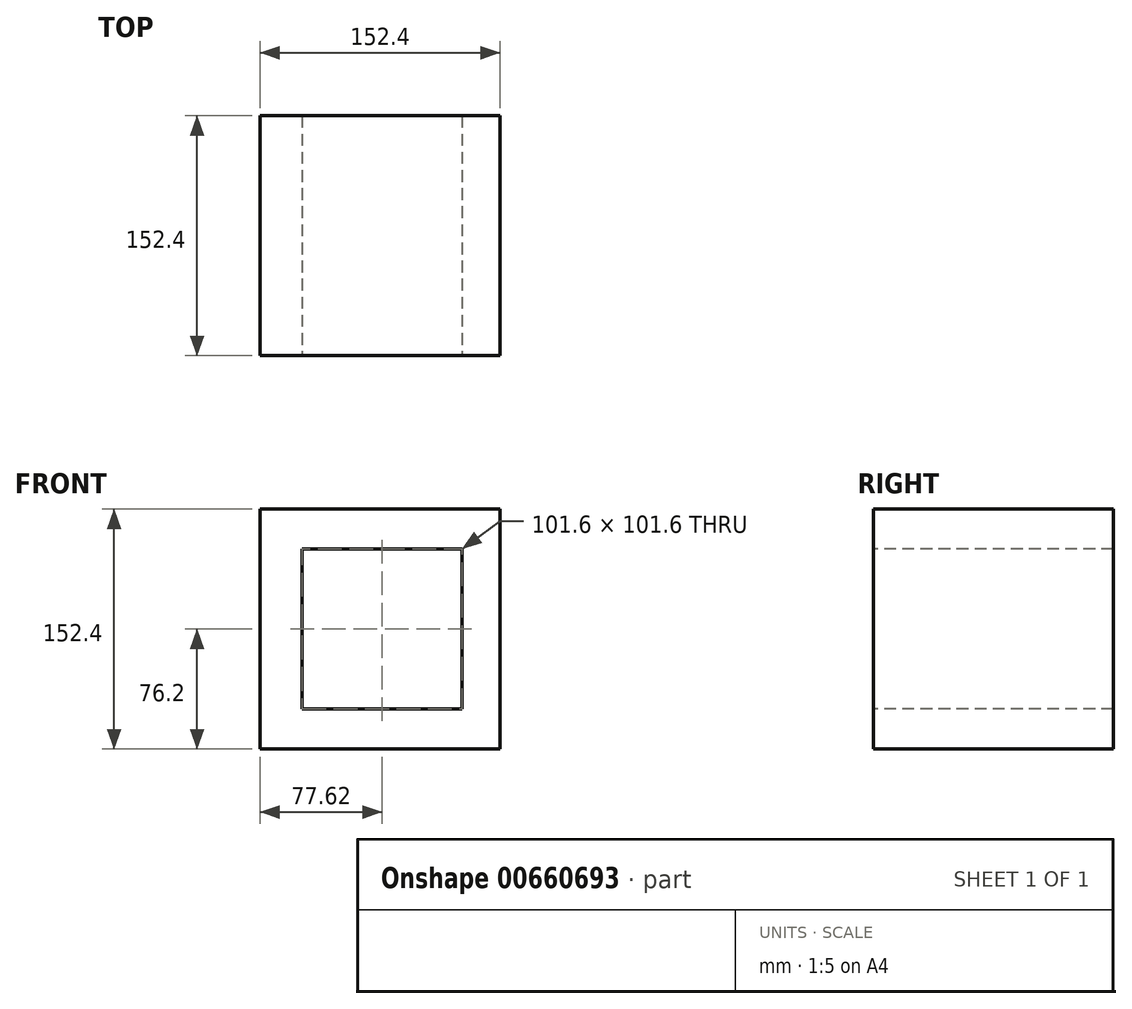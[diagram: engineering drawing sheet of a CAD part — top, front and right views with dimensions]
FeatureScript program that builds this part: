
annotation { "Feature Type Name" : "Feature", "Feature Type Description" : "" }
export const myFeature = defineFeature(function(context is Context, id is Id, definition is map)
    precondition{}
    {
        {
            var Q0;
            Q0=qCreatedBy(makeId("Top.planeOp"),FACE);
            var sketch = newSketch(context, id + "F0", { "sketchPlane" : qUnion([Q0])});
            skLineSegment(sketch, "E0", {"start": v(-77.62, 0) * mm, "end": v(74.78, 0) * mm});
            skLineSegment(sketch, "E1", {"start": v(74.78, 0) * mm, "end": v(74.78, 152.4) * mm});
            skLineSegment(sketch, "E2", {"start": v(74.78, 152.4) * mm, "end": v(-77.62, 152.4) * mm});
            skLineSegment(sketch, "E3", {"start": v(-77.62, 152.4) * mm, "end": v(-77.62, 0) * mm});
            skSolve(sketch);
        }
        {
            var Q0;
            Q0=makeQuery(id+"F0.imprint","IMPRINT",FACE,{"disambiguationData":[TD([[makeQuery(id+"F0.imprint","IMPRINT",EDGE,{"derivedFrom":sQuery(id+"F0.wireOp",EDGE,"E0")}),1.0]])]});
            extrude(context, id + "F1", {"entities" : qUnion([Q0]), "depth" : 152.4 * mm, "offsetDistance" : 25.4 * mm});
        }
        {
            var Q0;
            Q0=makeQuery(id+"F1.opExtrude","SWEPT_FACE",FACE,{"disambiguationData":[OSD([sQuery(id+"F0.wireOp",EDGE,"E0")])]});
            var sketch = newSketch(context, id + "F2", { "sketchPlane" : qUnion([Q0])});
            skLineSegment(sketch, "E4", {"start": v(0, 76.2) * mm, "end": v(0, 127) * mm});
            skLineSegment(sketch, "E5", {"start": v(0, 76.2) * mm, "end": v(50.8, 76.2) * mm});
            skLineSegment(sketch, "E6", {"start": v(0, 76.2) * mm, "end": v(-50.8, 76.2) * mm});
            skLineSegment(sketch, "E7", {"start": v(0, 76.2) * mm, "end": v(0, 25.4) * mm});
            skLineSegment(sketch, "E8", {"start": v(0, 127) * mm, "end": v(50.8, 127) * mm});
            skLineSegment(sketch, "E9", {"start": v(50.8, 127) * mm, "end": v(50.8, 76.2) * mm});
            skLineSegment(sketch, "E10", {"start": v(0, 25.4) * mm, "end": v(50.8, 25.4) * mm});
            skLineSegment(sketch, "E11", {"start": v(50.8, 25.4) * mm, "end": v(50.8, 76.2) * mm});
            skLineSegment(sketch, "E12", {"start": v(0, 127) * mm, "end": v(-50.8, 127) * mm});
            skLineSegment(sketch, "E13", {"start": v(-50.8, 127) * mm, "end": v(-50.8, 76.2) * mm});
            skLineSegment(sketch, "E14", {"start": v(-50.8, 76.2) * mm, "end": v(-50.8, 25.4) * mm});
            skLineSegment(sketch, "E15", {"start": v(-50.8, 25.4) * mm, "end": v(0, 25.4) * mm});
            skSolve(sketch);
        }
        {
            var Q0;
            Q0=makeQuery(id+"F2.imprint","IMPRINT",FACE,{"disambiguationData":[TD([[makeQuery(id+"F2.imprint","IMPRINT",EDGE,{"derivedFrom":sQuery(id+"F2.wireOp",EDGE,"E4")}),1.0]])]});
            var Q1;
            Q1=makeQuery(id+"F2.imprint","IMPRINT",FACE,{"disambiguationData":[TD([[makeQuery(id+"F2.imprint","IMPRINT",EDGE,{"derivedFrom":sQuery(id+"F2.wireOp",EDGE,"E4")}),-1.0]])]});
            var Q2;
            Q2=makeQuery(id+"F2.imprint","IMPRINT",FACE,{"disambiguationData":[TD([[makeQuery(id+"F2.imprint","IMPRINT",EDGE,{"derivedFrom":sQuery(id+"F2.wireOp",EDGE,"E5")}),-1.0]])]});
            var Q3;
            Q3=makeQuery(id+"F2.imprint","IMPRINT",FACE,{"disambiguationData":[TD([[makeQuery(id+"F2.imprint","IMPRINT",EDGE,{"derivedFrom":sQuery(id+"F2.wireOp",EDGE,"E6")}),1.0]])]});
            extrude(context, id + "F3", {"entities" : qUnion([Q0, Q1, Q2, Q3]), "operationType" : NewBodyOperationType.REMOVE, "oppositeDirection" : true, "depth" : 152.4 * mm, "offsetDistance" : 25.4 * mm});
        }
    });
